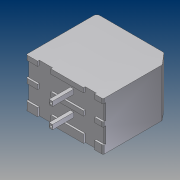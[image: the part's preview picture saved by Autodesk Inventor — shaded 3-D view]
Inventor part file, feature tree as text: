
AUTODESK INVENTOR PART (.ipt)
format: ipt  version: unknown  size: 359,424 bytes
history: native  units: mm (DEFAULTED — no unit token found)
features: sketch x20, extrude x19, pattern_linear x9, revolve x1
ambient origin geometry x8: Origin, YZ Plane, XZ Plane, XY Plane, X Axis, Y Axis, Z Axis, Center Point
feature tree (49):
  extrude  "Extrusion1"  Depth=0.8mm TaperAngle=0.0deg
  extrude  "Extrusion2"  Depth=0.8mm TaperAngle=0.0deg
  pattern_linear  "Rectangular Pattern1"  Count1=2 Spacing1=3.5mm
  extrude  "Extrusion3"  Depth=20.0mm TaperAngle=0.0deg
  pattern_linear  "Rectangular Pattern2"  Count1=2 Spacing1=3.5mm
  extrude  "Extrusion4"  Depth=20.0mm TaperAngle=0.0deg
  pattern_linear  "Rectangular Pattern3"  Count1=2 Spacing1=3.5mm
  extrude  "Extrusion5"  TaperAngle=360.0deg  [1 undecoded]
  extrude  "Extrusion6"  Depth=1.0mm TaperAngle=0.0deg
  extrude  "Extrusion7"  Depth=3.7mm TaperAngle=0.0deg
  extrude  "Extrusion8"  Depth=0.5mm
  extrude  "Extrusion9"  [1 undecoded]
  extrude  "Extrusion10"  [1 undecoded]
  extrude  "Extrusion11"  [1 undecoded]
  extrude  "Extrusion12"  [1 undecoded]
  extrude  "Extrusion13"  [1 undecoded]
  pattern_linear  "Rectangular Pattern4"  [2 undecoded]
  extrude  "Extrusion14"  [1 undecoded]
  pattern_linear  "Rectangular Pattern5"  [2 undecoded]
  extrude  "Extrusion15"  [1 undecoded]
  pattern_linear  "Rectangular Pattern6"  [2 undecoded]
  extrude  "Extrusion16"  [1 undecoded]
  revolve  "Revolution1"  [1 undecoded]
  pattern_linear  "Rectangular Pattern7"  [2 undecoded]
  extrude  "Extrusion17"  [1 undecoded]
  pattern_linear  "Rectangular Pattern8"  [2 undecoded]
  extrude  "Extrusion18"  [1 undecoded]
  pattern_linear  "Rectangular Pattern9"  [2 undecoded]
  extrude  "Extrusion19"  [1 undecoded]
  sketch  "Skizze_1"  dims[d0=7.0mm d1=0.0mm d2=0.8mm d3=0.0mm]
  sketch  "Skizze_2"  dims[d4=20.0mm d6=3.5mm d7=10.0mm d9=0.0mm d10=0.8mm d11=0.0mm d12=20.0mm d14=3.5mm d15=10.0mm d17=0.0mm]
  sketch  "Skizze_4"  dims[d18=0.8mm d19=0.0mm d20=20.0mm d22=3.5mm d23=10.0mm d25=0.0mm]
  sketch  "Skizze_6"  dims[d26=1.5mm d27=0.0mm]
  sketch  "Skizze_8"  dims[d28=1.5mm d29=0.0mm]
  sketch  "Skizze_9"  dims[d30=1.5mm d31=0.0mm]
  sketch  "Skizze_10"  dims[d32=1.5mm d33=0.0mm]
  sketch  "Skizze_11"  dims[d34=1.5mm d35=0.0mm]
  sketch  "Skizze_12"  dims[d36=1.5mm d37=0.0mm]
  sketch  "Skizze_13"  dims[d38=1.5mm d39=0.0mm]
  sketch  "Skizze_14"  dims[d40=1.4mm d41=0.0mm]
  sketch  "Skizze_15"  dims[d42=3.2mm d43=0.0mm d44=20.0mm d46=3.5mm d47=10.0mm d49=0.0mm]
  sketch  "Skizze_16"  dims[d50=6.0mm d51=0.0mm d52=20.0mm d54=3.5mm d55=10.0mm d57=0.0mm]
  sketch  "Skizze_18"  dims[d58=4.1mm d59=0.0mm d60=20.0mm d62=3.5mm d63=10.0mm d65=0.0mm]
  sketch  "Skizze_20"  dims[d66=7.0mm d67=0.0mm d68=360.0deg]
  sketch  "Skizze_22"  dims[d77=20.0mm d79=3.5mm d80=10.0mm d82=0.0mm d83=3.7mm d84=0.0mm]
  sketch  "Skizze_23"  dims[d85=20.0mm d87=3.5mm d88=10.0mm d90=0.0mm d91=0.5mm]
  sketch  "Skizze_24"  dims[d92=0.5mm d93=0.0mm]
  sketch  "Skizze_27"
  sketch  "Sketch20"  dims[d69=20.0mm d71=3.5mm d72=10.0mm d74=0.0mm d75=1.0mm d76=0.0mm]
note: 25 required parameter values undecoded (feature->parameter linkage not recoverable at this tier; creation-order binding heuristic only, values carry confidence <= 0.55)
